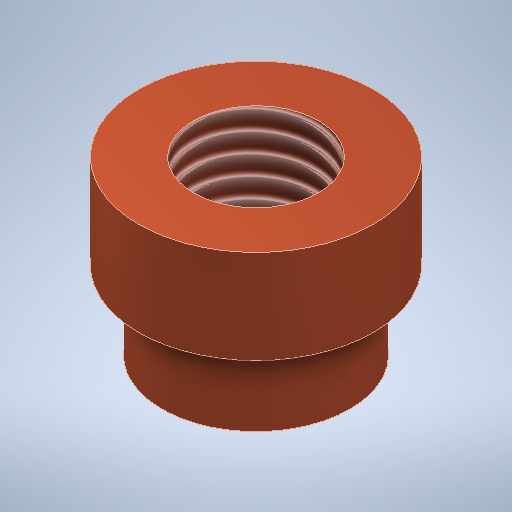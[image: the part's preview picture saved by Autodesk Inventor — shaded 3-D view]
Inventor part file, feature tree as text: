
AUTODESK INVENTOR PART (.ipt)
format: ipt  version: 2025.1 (Build 291241000, 241)  size: 272,896 bytes
history: native  units: mm
features: sketch x3, extrude x2, hole x1, thread x1
ambient origin geometry x8: Origin, YZ Plane, XZ Plane, XY Plane, X Axis, Y Axis, Z Axis, Center Point
bodies: Solid1 (feature_tree)
feature tree (7):
  extrude  "Extrusion1"  Depth=6.0mm TaperAngle=0.0deg
  extrude  "Extrusion2"  Depth=5.0mm TaperAngle=0.0deg
  hole  "Hole1"  [1 undecoded]
  thread  "Thread1"  [1 undecoded]
  sketch  "Sketch1"  dims[d0=15.0mm d1=6.0mm d2=0.0mm]
  sketch  "Sketch2"  dims[d3=12.0mm d4=5.0mm d5=0.0mm]
  sketch  "Sketch3"  dims[d6=8.0mm d7=16.0mm d8=4.0mm d9=2.0mm d10=90.0deg d11=22.2mm d12=0.0mm d13=15.0mm d14=0.0mm]
note: 2 required parameter values undecoded (feature->parameter linkage not recoverable at this tier; creation-order binding heuristic only, values carry confidence <= 0.55)
